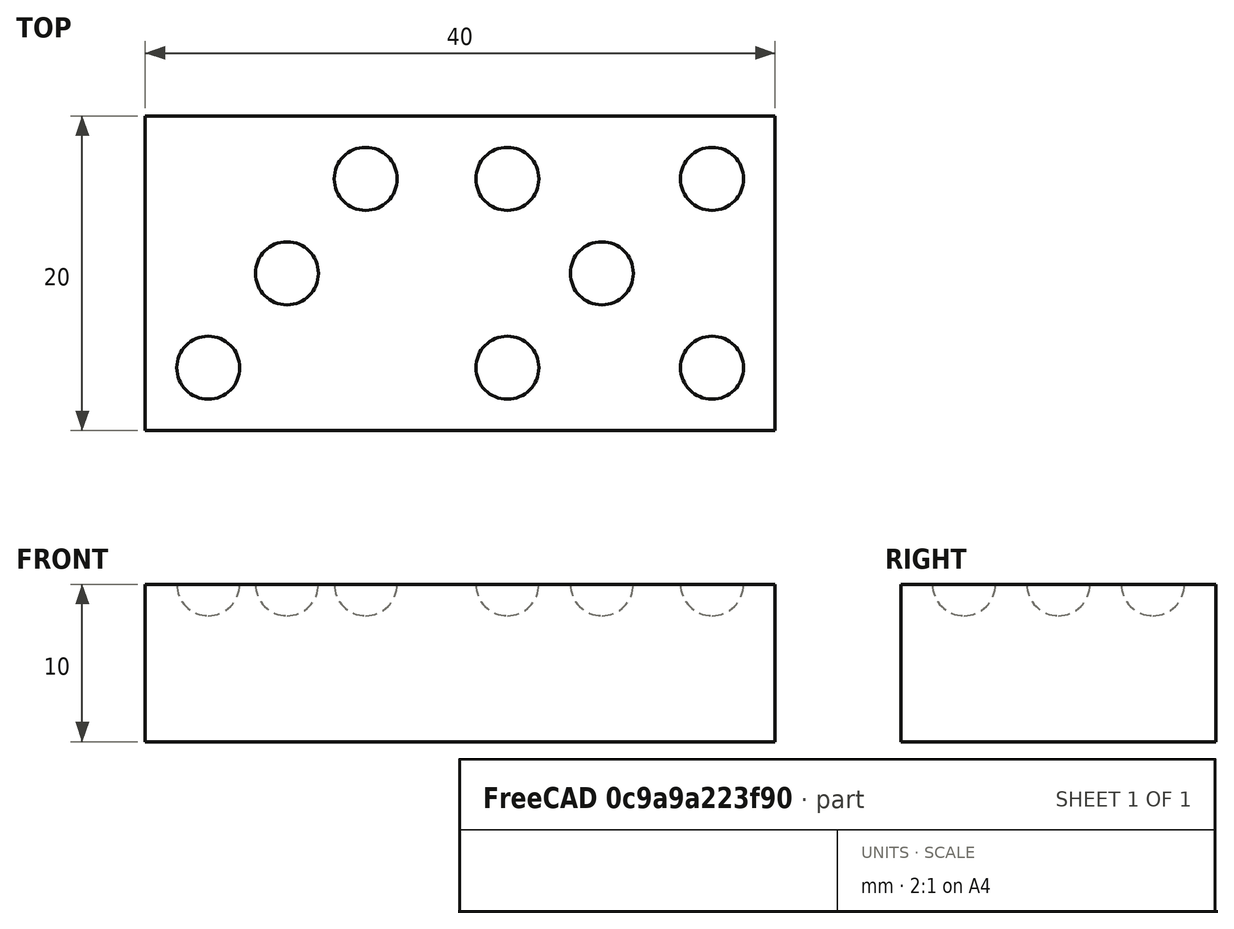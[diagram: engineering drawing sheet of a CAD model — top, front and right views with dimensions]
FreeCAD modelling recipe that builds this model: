
FCSTD DOCUMENT  (FreeCAD 0.21R33694 (Git))
Label: OJT1_T013R012_DOMINO
License: All rights reserved
LicenseURL: http://en.wikipedia.org/wiki/All_rights_reserved
objects: Part::Sphere×8, Part::Cut×3, Part::Box×2, Part::MultiFuse×2
note: 15 computed .brp shape members not serialized (recipe doc carries the construction recipe); baked Part::Feature solids carry a one-line shape summary decoded from their .brp

FEATURE [Part::Box] Box  label="Cube"
  AttacherType = Attacher::AttachEngine3D
  Height = 10
  Length = 40
  Width = 20
FEATURE [Part::Sphere] Sphere
  Angle1 = -90
  Angle2 = 90
  Angle3 = 360
  AttacherType = Attacher::AttachEngine3D
  Placement = pos=(4,4,10) rot=(0,0,1;0rad)
  Radius = 2
FEATURE [Part::Sphere] Sphere001
  Angle1 = -90
  Angle2 = 90
  Angle3 = 360
  AttacherType = Attacher::AttachEngine3D
  Placement = pos=(9,10,10) rot=(0,0,1;0rad)
  Radius = 2
FEATURE [Part::Sphere] Sphere002
  Angle1 = -90
  Angle2 = 90
  Angle3 = 360
  AttacherType = Attacher::AttachEngine3D
  Placement = pos=(14,16,10) rot=(0,0,1;0rad)
  Radius = 2
FEATURE [Part::Box] Box001  label="Cube001"
  AttacherType = Attacher::AttachEngine3D
  Height = 6
  Length = 1
  Placement = pos=(18,1,5) rot=(0,0,1;0rad)
  Width = 18
FEATURE [Part::MultiFuse] Fusion
  Refine = true
  Shapes = -> [Sphere002,Sphere001,Sphere]
FEATURE [Part::Sphere] Sphere003
  Angle1 = -90
  Angle2 = 90
  Angle3 = 360
  AttacherType = Attacher::AttachEngine3D
  Placement = pos=(29,10,10) rot=(0,0,1;0rad)
  Radius = 2
FEATURE [Part::Sphere] Sphere004
  Angle1 = -90
  Angle2 = 90
  Angle3 = 360
  AttacherType = Attacher::AttachEngine3D
  Placement = pos=(23,4,10) rot=(0,0,1;0rad)
  Radius = 2
FEATURE [Part::Sphere] Sphere005
  Angle1 = -90
  Angle2 = 90
  Angle3 = 360
  AttacherType = Attacher::AttachEngine3D
  Placement = pos=(36,4,10) rot=(0,0,1;0rad)
  Radius = 2
FEATURE [Part::Sphere] Sphere006
  Angle1 = -90
  Angle2 = 90
  Angle3 = 360
  AttacherType = Attacher::AttachEngine3D
  Placement = pos=(23,16,10) rot=(0,0,1;0rad)
  Radius = 2
FEATURE [Part::Sphere] Sphere007
  Angle1 = -90
  Angle2 = 90
  Angle3 = 360
  AttacherType = Attacher::AttachEngine3D
  Placement = pos=(36,16,10) rot=(0,0,1;0rad)
  Radius = 2
FEATURE [Part::MultiFuse] Fusion001
  Refine = true
  Shapes = -> [Sphere003,Sphere004,Sphere005,Sphere006,Sphere007]
FEATURE [Part::Cut] Cut
  Base = -> Box
  Refine = true
  Tool = -> Box001
FEATURE [Part::Cut] Cut001
  Base = -> Box
  Refine = true
  Tool = -> Fusion001
FEATURE [Part::Cut] Cut002
  Base = -> Box
  Refine = true
  Tool = -> Fusion
